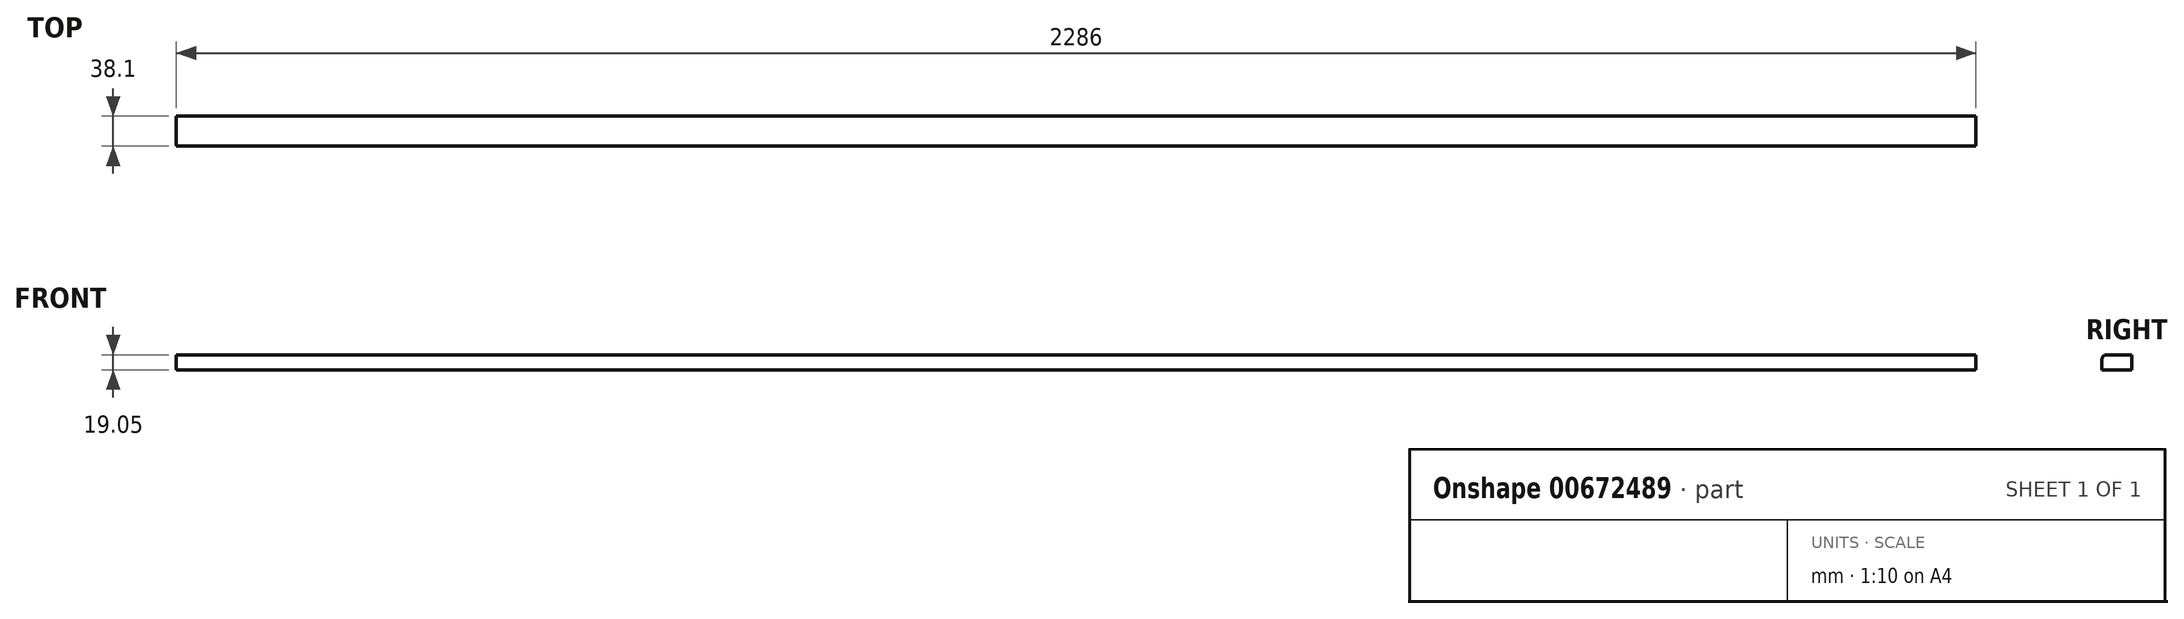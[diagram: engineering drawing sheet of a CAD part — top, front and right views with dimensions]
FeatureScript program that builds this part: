
annotation { "Feature Type Name" : "Feature", "Feature Type Description" : "" }
export const myFeature = defineFeature(function(context is Context, id is Id, definition is map)
    precondition{}
    {
        {
            var Q0;
            Q0=qCreatedBy(makeId("Top.planeOp"),FACE);
            var sketch = newSketch(context, id + "F0", { "sketchPlane" : qUnion([Q0])});
            skLineSegment(sketch, "E0.bottom", {"start": v(-1143, 19.05) * mm, "end": v(1143, 19.05) * mm});
            skLineSegment(sketch, "E0.top", {"start": v(-1143, -19.05) * mm, "end": v(1143, -19.05) * mm});
            skLineSegment(sketch, "E0.left", {"start": v(-1143, 19.05) * mm, "end": v(-1143, -19.05) * mm});
            skLineSegment(sketch, "E0.right", {"start": v(1143, 19.05) * mm, "end": v(1143, -19.05) * mm});
            skPoint(sketch, "E1", {"position": v(0, -19.05) * mm});
            skPoint(sketch, "E2", {"position": v(1143, 0) * mm});
            skSolve(sketch);
        }
        {
            var Q0;
            Q0=makeQuery(id+"F0.imprint","IMPRINT",FACE,{"disambiguationData":[TD([[makeQuery(id+"F0.imprint","IMPRINT",EDGE,{"derivedFrom":sQuery(id+"F0.wireOp",EDGE,"E0.bottom")}),-1.0]])]});
            extrude(context, id + "F1", {"entities" : qUnion([Q0]), "depth" : 19.05 * mm, "offsetDistance" : 25.4 * mm});
        }
        {
            var Q0;
            Q0=makeQuery(id+"F1.opExtrude","CAP_EDGE",EDGE,{"disambiguationData":[OSD([sQuery(id+"F0.wireOp",EDGE,"E0.top")])],"isStart":false});
            fillet(context, id + "F2", {"entities" : qUnion([Q0]), "radius" : 6.35 * mm, "tangentPropagation" : true, "allowEdgeOverflow" : false});
        }
    });
